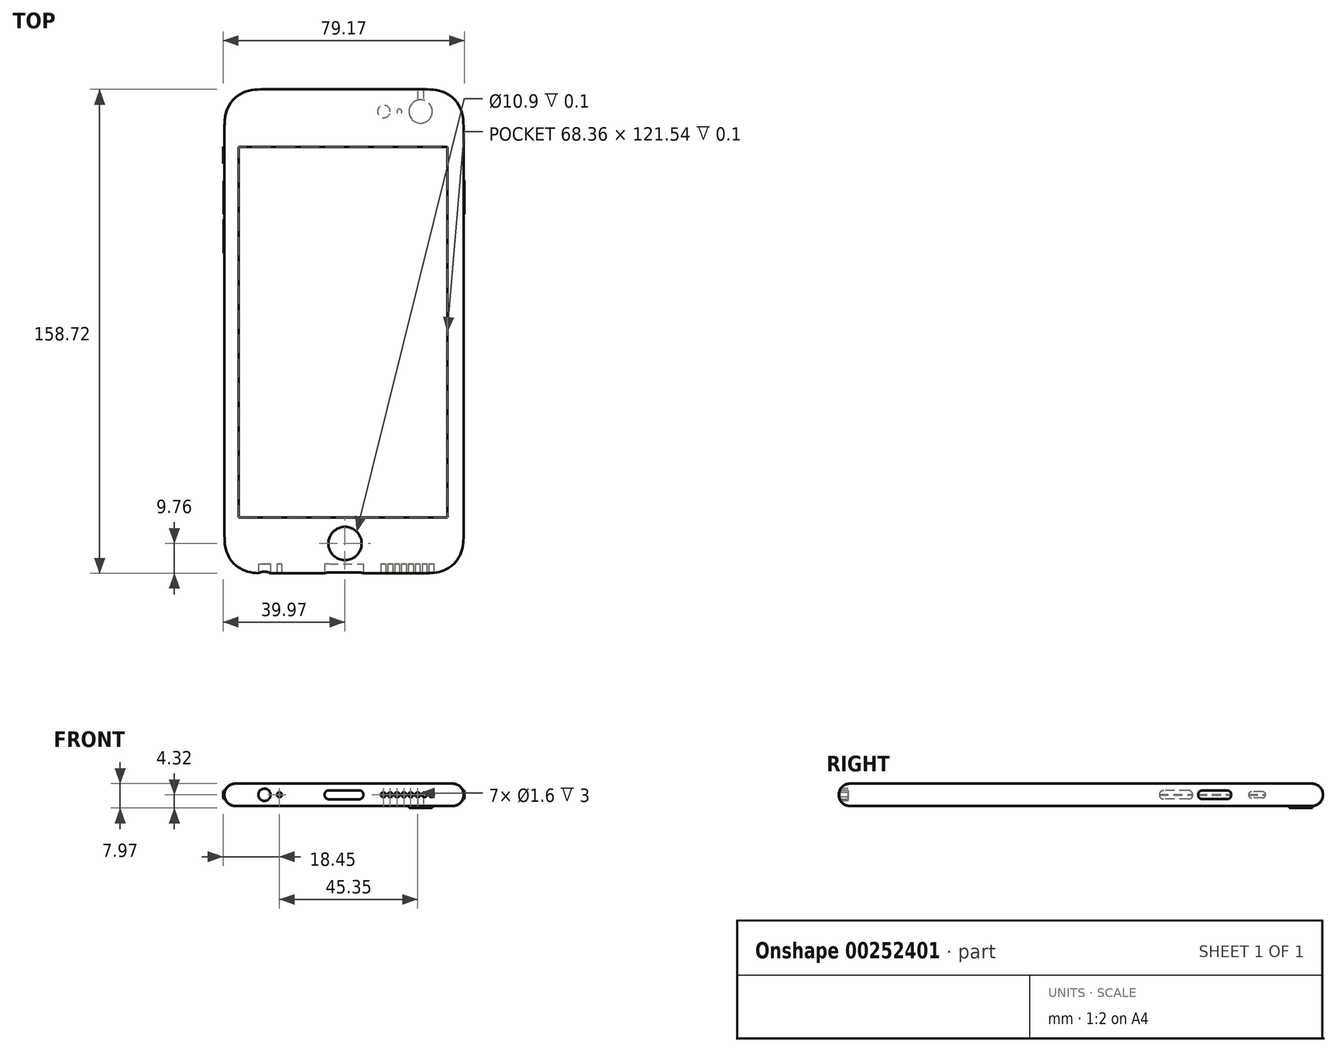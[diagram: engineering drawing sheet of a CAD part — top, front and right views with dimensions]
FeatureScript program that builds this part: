
annotation { "Feature Type Name" : "Feature", "Feature Type Description" : "" }
export const myFeature = defineFeature(function(context is Context, id is Id, definition is map)
    precondition{}
    {
        {
            var Q0;
            Q0=qCreatedBy(makeId("Top.planeOp"),FACE);
            var sketch = newSketch(context, id + "F0", { "sketchPlane" : qUnion([Q0])});
            skLineSegment(sketch, "E0.rect.bottom", {"start": v(25.09, -79.36) * mm, "end": v(-25.09, -79.36) * mm});
            skLineSegment(sketch, "E0.rect.top", {"start": v(25.09, 79.36) * mm, "end": v(-25.09, 79.36) * mm});
            skLineSegment(sketch, "E0.rect.left", {"start": v(39.22, -65.23) * mm, "end": v(39.22, 65.23) * mm});
            skLineSegment(sketch, "E0.rect.right", {"start": v(-39.22, -65.23) * mm, "end": v(-39.22, 65.23) * mm});
            skPoint(sketch, "E0.rect.middle", {"position": v(0, 0) * mm});
            skCircle(sketch, "E1", {"center": v(25.12, 72.09) * mm, "radius": 3.83 * mm});
            skCircle(sketch, "E2", {"center": v(18.16, 72.09) * mm, "radius": 0.8 * mm});
            skCircle(sketch, "E3", {"center": v(13.06, 72.09) * mm, "radius": 2.06 * mm});
            skLineSegment(sketch, "E4", {"start": v(-39.22, 72.1) * mm, "end": v(39.22, 72.1) * mm, "construction": true});
            skPoint(sketch, "E5.visualSharp", {"position": v(-39.22, 79.36) * mm});
            skFitSpline(sketch, "E6", {"points": [v(-25.09, 79.36) * mm, v(-29.02, 79.25) * mm, v(-32.83, 78.38) * mm, v(-36.09, 76.23) * mm, v(-38.24, 72.97) * mm, v(-39.1, 69.16) * mm, v(-39.22, 65.23) * mm], "startDerivative": vector(-8.98, 0) * mm, "endDerivative": vector(0, -8.98) * mm});
            skLineSegment(sketch, "E7", {"start": v(-25.09, 79.36) * mm, "end": v(-39.22, 79.36) * mm, "construction": true});
            skLineSegment(sketch, "E8", {"start": v(-39.22, 79.36) * mm, "end": v(-39.22, 65.23) * mm, "construction": true});
            skLineSegment(sketch, "E9", {"start": v(0, 79.36) * mm, "end": v(0, -79.36) * mm, "construction": true});
            skLineSegment(sketch, "E10", {"start": v(-39.22, 0) * mm, "end": v(39.22, 0) * mm, "construction": true});
            skFitSpline(sketch, "E11.MirrorCS", {"points": [v(25.09, 79.36) * mm, v(29.02, 79.25) * mm, v(32.83, 78.38) * mm, v(36.09, 76.23) * mm, v(38.24, 72.97) * mm, v(39.1, 69.16) * mm, v(39.22, 65.23) * mm], "startDerivative": vector(8.98, 0) * mm, "endDerivative": vector(0, -8.98) * mm});
            skFitSpline(sketch, "E12.MirrorCS", {"points": [v(-25.09, -79.36) * mm, v(-29.02, -79.25) * mm, v(-32.83, -78.38) * mm, v(-36.09, -76.23) * mm, v(-38.24, -72.97) * mm, v(-39.1, -69.16) * mm, v(-39.22, -65.23) * mm], "startDerivative": vector(-8.98, 0) * mm, "endDerivative": vector(0, 8.98) * mm});
            skFitSpline(sketch, "E13.MirrorCS", {"points": [v(25.09, -79.36) * mm, v(29.02, -79.25) * mm, v(32.83, -78.38) * mm, v(36.09, -76.23) * mm, v(38.24, -72.97) * mm, v(39.1, -69.16) * mm, v(39.22, -65.23) * mm], "startDerivative": vector(8.98, 0) * mm, "endDerivative": vector(0, 8.98) * mm});
            skCircle(sketch, "E14", {"center": v(0, 37.36) * mm, "radius": 11 * mm, "construction": true});
            skSolve(sketch);
        }
        {
            var Q0;
            Q0=makeQuery(id+"F0.imprint","IMPRINT",FACE,{"disambiguationData":[TD([[makeQuery(id+"F0.imprint","IMPRINT",EDGE,{"derivedFrom":sQuery(id+"F0.wireOp",EDGE,"E0.rect.bottom")}),-1.0]])]});
            var Q1;
            Q1=makeQuery(id+"F0.imprint","IMPRINT",FACE,{"disambiguationData":[TD([[makeQuery(id+"F0.imprint","IMPRINT",EDGE,{"derivedFrom":sQuery(id+"F0.wireOp",EDGE,"E1")}),1.0]])]});
            var Q2;
            Q2=makeQuery(id+"F0.imprint","IMPRINT",FACE,{"disambiguationData":[TD([[makeQuery(id+"F0.imprint","IMPRINT",EDGE,{"derivedFrom":sQuery(id+"F0.wireOp",EDGE,"E2")}),1.0]])]});
            var Q3;
            Q3=makeQuery(id+"F0.imprint","IMPRINT",FACE,{"disambiguationData":[TD([[makeQuery(id+"F0.imprint","IMPRINT",EDGE,{"derivedFrom":sQuery(id+"F0.wireOp",EDGE,"E3")}),1.0]])]});
            extrude(context, id + "F1", {"entities" : qUnion([Q0, Q1, Q2, Q3]), "depth" : 7.3 * mm});
        }
        {
            var Q0;
            Q0=makeQuery(id+"F0.imprint","IMPRINT",FACE,{"disambiguationData":[TD([[makeQuery(id+"F0.imprint","IMPRINT",EDGE,{"derivedFrom":sQuery(id+"F0.wireOp",EDGE,"E1")}),1.0]])]});
            extrude(context, id + "F2", {"entities" : qUnion([Q0]), "operationType" : NewBodyOperationType.ADD, "oppositeDirection" : true, "depth" : 0.67 * mm});
        }
        {
            var Q0;
            Q0=makeQuery(id+"F0.imprint","IMPRINT",FACE,{"disambiguationData":[TD([[makeQuery(id+"F0.imprint","IMPRINT",EDGE,{"derivedFrom":sQuery(id+"F0.wireOp",EDGE,"E3")}),1.0]])]});
            var Q1;
            Q1=makeQuery(id+"F0.imprint","IMPRINT",FACE,{"disambiguationData":[TD([[makeQuery(id+"F0.imprint","IMPRINT",EDGE,{"derivedFrom":sQuery(id+"F0.wireOp",EDGE,"E2")}),1.0]])]});
            extrude(context, id + "F3", {"entities" : qUnion([Q0, Q1]), "operationType" : NewBodyOperationType.REMOVE, "depth" : 0.1 * mm});
        }
        {
            var Q0;
            Q0=makeQuery(id+"F1.opExtrude","CAP_FACE",FACE,{"disambiguationData":[OSD([sQuery(id+"F0.wireOp",EDGE,"E0.rect.bottom"),sQuery(id+"F0.wireOp",EDGE,"E0.rect.top"),sQuery(id+"F0.wireOp",EDGE,"E0.rect.left"),sQuery(id+"F0.wireOp",EDGE,"E0.rect.right"),sQuery(id+"F0.wireOp",EDGE,"d7852d5b-fe0f-4a90-bdf2-04cff158e1f8.filletArc"),sQuery(id+"F0.wireOp",EDGE,"E5.filletArc"),sQuery(id+"F0.wireOp",EDGE,"7c06d2e9-cdf6-4879-9dee-aab3bc7c6033.filletArc"),sQuery(id+"F0.wireOp",EDGE,"93b3bdb9-dbb8-49f8-8f1e-002f612095da.filletArc")])],"isStart":false});
            var sketch = newSketch(context, id + "F4", { "sketchPlane" : qUnion([Q0])});
            skCircle(sketch, "E15", {"center": v(0.32, -69.6) * mm, "radius": 5.45 * mm});
            skLineSegment(sketch, "E16.bottom", {"start": v(-34.51, 60.44) * mm, "end": v(33.85, 60.44) * mm});
            skLineSegment(sketch, "E16.top", {"start": v(-34.5, -61.1) * mm, "end": v(33.85, -61.1) * mm});
            skLineSegment(sketch, "E16.left", {"start": v(-34.51, 60.44) * mm, "end": v(-34.5, -61.1) * mm});
            skLineSegment(sketch, "E16.right", {"start": v(33.85, 60.44) * mm, "end": v(33.85, -61.1) * mm});
            skSolve(sketch);
        }
        {
            var Q0;
            Q0=makeQuery(id+"F4.imprint","IMPRINT",FACE,{"disambiguationData":[TD([[makeQuery(id+"F4.imprint","IMPRINT",EDGE,{"derivedFrom":sQuery(id+"F4.wireOp",EDGE,"E15")}),1.0]])]});
            extrude(context, id + "F5", {"entities" : qUnion([Q0]), "operationType" : NewBodyOperationType.REMOVE, "oppositeDirection" : true, "depth" : 0.1 * mm});
        }
        {
            var Q0;
            Q0=makeQuery(id+"F4.imprint","IMPRINT",FACE,{"disambiguationData":[TD([[makeQuery(id+"F4.imprint","IMPRINT",EDGE,{"derivedFrom":sQuery(id+"F4.wireOp",EDGE,"E16.bottom")}),-1.0]])]});
            extrude(context, id + "F6", {"entities" : qUnion([Q0]), "operationType" : NewBodyOperationType.REMOVE, "oppositeDirection" : true, "depth" : 0.1 * mm});
        }
        {
            var Q0;
            Q0=makeQuery(id+"F1.opExtrude","SWEPT_FACE",FACE,{"disambiguationData":[OSD([sQuery(id+"F0.wireOp",EDGE,"E0.rect.bottom")])]});
            var sketch = newSketch(context, id + "F7", { "sketchPlane" : qUnion([Q0])});
            skLineSegment(sketch, "E17.0", {"start": v(25.09, 7.3) * mm, "end": v(-25.09, 7.3) * mm, "construction": true});
            skLineSegment(sketch, "E17.1", {"start": v(25.09, 0) * mm, "end": v(-25.09, 0) * mm, "construction": true});
            skLineSegment(sketch, "E17.2", {"start": v(39.22, 7.3) * mm, "end": v(39.22, 0) * mm, "construction": true});
            skLineSegment(sketch, "E17.3", {"start": v(-39.22, 7.3) * mm, "end": v(-39.22, 0) * mm, "construction": true});
            skFitSpline(sketch, "E17.4", {"points": [v(-24.74, 7.3) * mm, v(-29.45, 7.3) * mm, v(-34.16, 7.3) * mm, v(-38.87, 7.3) * mm], "construction": true});
            skFitSpline(sketch, "E17.5", {"points": [v(-24.74, 0) * mm, v(-29.45, 0) * mm, v(-34.16, 0) * mm, v(-38.87, 0) * mm], "construction": true});
            skFitSpline(sketch, "E17.6", {"points": [v(24.74, 0) * mm, v(29.45, 0) * mm, v(34.16, 0) * mm, v(38.87, 0) * mm], "construction": true});
            skFitSpline(sketch, "E17.7", {"points": [v(24.74, 7.3) * mm, v(29.45, 7.3) * mm, v(34.16, 7.3) * mm, v(38.87, 7.3) * mm], "construction": true});
            skLineSegment(sketch, "E18", {"start": v(0, 7.3) * mm, "end": v(0, 0) * mm, "construction": true});
            skLineSegment(sketch, "E19", {"start": v(-39.22, 3.65) * mm, "end": v(-6.4, 3.65) * mm, "construction": true});
            skLineSegment(sketch, "E20", {"start": v(-4.92, 5.12) * mm, "end": v(4.92, 5.12) * mm});
            skLineSegment(sketch, "E21", {"start": v(-4.92, 2.17) * mm, "end": v(4.92, 2.17) * mm});
            skLineSegment(sketch, "E22", {"start": v(-6.4, 3.65) * mm, "end": v(39.22, 3.65) * mm, "construction": true});
            skArc(sketch, "E23", {"start": v(-4.92, 5.13) * mm, "mid": v(-6.4, 3.65) * mm, "end": v(-4.92, 2.17) * mm});
            skArc(sketch, "E24", {"start": v(-4.92, 2.17) * mm, "mid": v(-3.44, 3.65) * mm, "end": v(-4.92, 5.13) * mm, "construction": true});
            skArc(sketch, "E25", {"start": v(4.92, 5.13) * mm, "mid": v(5.96, 4.7) * mm, "end": v(6.4, 3.65) * mm});
            skArc(sketch, "E26", {"start": v(4.92, 2.17) * mm, "mid": v(3.44, 3.65) * mm, "end": v(4.92, 5.13) * mm, "construction": true});
            skArc(sketch, "E27", {"start": v(6.4, 3.65) * mm, "mid": v(5.96, 2.6) * mm, "end": v(4.92, 2.17) * mm});
            skCircle(sketch, "E28", {"center": v(-26.09, 3.65) * mm, "radius": 2 * mm});
            skCircle(sketch, "E29", {"center": v(-21.2, 3.65) * mm, "radius": 0.8 * mm});
            skCircle(sketch, "E30", {"center": v(12.9, 3.65) * mm, "radius": 0.8 * mm});
            skCircle(sketch, "E31.1.0.0", {"center": v(15.15, 3.65) * mm, "radius": 0.8 * mm});
            skCircle(sketch, "E31.2.0.0", {"center": v(17.4, 3.65) * mm, "radius": 0.8 * mm});
            skCircle(sketch, "E31.3.0.0", {"center": v(19.65, 3.65) * mm, "radius": 0.8 * mm});
            skCircle(sketch, "E31.4.0.0", {"center": v(21.9, 3.65) * mm, "radius": 0.8 * mm});
            skCircle(sketch, "E31.5.0.0", {"center": v(24.15, 3.65) * mm, "radius": 0.8 * mm});
            skCircle(sketch, "E31.6.0.0", {"center": v(26.4, 3.65) * mm, "radius": 0.8 * mm});
            skCircle(sketch, "E31.7.0.0", {"center": v(28.65, 3.65) * mm, "radius": 0.8 * mm});
            skLineSegment(sketch, "E31.direction1", {"start": v(12.9, 3.65) * mm, "end": v(15.15, 3.65) * mm, "construction": true});
            skPoint(sketch, "E32", {"position": v(12.1, 3.65) * mm});
            skPoint(sketch, "E33", {"position": v(29.45, 3.65) * mm});
            skLineSegment(sketch, "E34.0", {"start": v(-25.09, 7.3) * mm, "end": v(-25.09, 0) * mm, "construction": true});
            skLineSegment(sketch, "E34.1", {"start": v(25.09, 7.3) * mm, "end": v(25.09, 0) * mm, "construction": true});
            skSolve(sketch);
        }
        {
            var Q0;
            Q0=makeQuery(id+"F1.opExtrude","SWEPT_FACE",FACE,{"disambiguationData":[OSD([sQuery(id+"F0.wireOp",EDGE,"E0.rect.left")])]});
            var sketch = newSketch(context, id + "F8", { "sketchPlane" : qUnion([Q0])});
            skLineSegment(sketch, "E35", {"start": v(-65.23, 2.25) * mm, "end": v(65.23, 2.25) * mm, "construction": true});
            skLineSegment(sketch, "E36", {"start": v(8.97, 4.69) * mm, "end": v(22.34, 4.7) * mm});
            skLineSegment(sketch, "E37", {"start": v(8.97, 2.25) * mm, "end": v(22.34, 2.25) * mm});
            skPoint(sketch, "E38", {"position": v(7.75, 3.47) * mm});
            skPoint(sketch, "E39", {"position": v(23.56, 3.47) * mm});
            skLineSegment(sketch, "E40", {"start": v(39.81, 2.25) * mm, "end": v(47.95, 2.25) * mm});
            skLineSegment(sketch, "E41", {"start": v(39.81, 5.05) * mm, "end": v(39.81, 5.05) * mm});
            skLineSegment(sketch, "E42", {"start": v(39.81, 3.65) * mm, "end": v(47.95, 3.65) * mm, "construction": true});
            skLineSegment(sketch, "E43", {"start": v(39.81, 5.05) * mm, "end": v(47.95, 5.05) * mm});
            skArc(sketch, "E44", {"start": v(47.95, 5.05) * mm, "mid": v(46.55, 3.65) * mm, "end": v(47.95, 2.25) * mm, "construction": true});
            skArc(sketch, "E45", {"start": v(47.95, 2.25) * mm, "mid": v(49.35, 3.65) * mm, "end": v(47.95, 5.05) * mm});
            skArc(sketch, "E46", {"start": v(39.81, 2.25) * mm, "mid": v(41.21, 3.65) * mm, "end": v(39.81, 5.05) * mm, "construction": true});
            skArc(sketch, "E47", {"start": v(39.81, 5.05) * mm, "mid": v(38.41, 3.65) * mm, "end": v(39.81, 2.25) * mm});
            skPoint(sketch, "E48", {"position": v(43.88, 3.65) * mm});
            skPoint(sketch, "E49", {"position": v(38.4, 3.65) * mm});
            skArc(sketch, "E50", {"start": v(8.97, 4.7) * mm, "mid": v(7.75, 3.47) * mm, "end": v(8.97, 2.25) * mm});
            skArc(sketch, "E51", {"start": v(8.97, 2.25) * mm, "mid": v(10.2, 3.47) * mm, "end": v(8.97, 4.7) * mm, "construction": true});
            skArc(sketch, "E52", {"start": v(22.34, 4.7) * mm, "mid": v(21.12, 3.47) * mm, "end": v(22.34, 2.25) * mm, "construction": true});
            skArc(sketch, "E53", {"start": v(22.34, 2.25) * mm, "mid": v(23.56, 3.47) * mm, "end": v(22.34, 4.7) * mm});
            skSolve(sketch);
        }
        {
            var Q0;
            Q0=makeQuery(id+"F1.opExtrude","SWEPT_FACE",FACE,{"disambiguationData":[OSD([sQuery(id+"F0.wireOp",EDGE,"E0.rect.right")])]});
            var sketch = newSketch(context, id + "F9", { "sketchPlane" : qUnion([Q0])});
            skLineSegment(sketch, "E54", {"start": v(-65.23, 3.63) * mm, "end": v(65.23, 3.63) * mm, "construction": true});
            skLineSegment(sketch, "E55", {"start": v(-60.58, 3.65) * mm, "end": v(-54.97, 3.65) * mm, "construction": true});
            skLineSegment(sketch, "E56", {"start": v(-59.6, 2.66) * mm, "end": v(-55.95, 2.66) * mm});
            skLineSegment(sketch, "E57", {"start": v(-59.6, 4.63) * mm, "end": v(-55.95, 4.63) * mm});
            skArc(sketch, "E58", {"start": v(-59.6, 2.66) * mm, "mid": v(-58.61, 3.64) * mm, "end": v(-59.6, 4.63) * mm, "construction": true});
            skArc(sketch, "E59", {"start": v(-59.6, 4.63) * mm, "mid": v(-60.58, 3.64) * mm, "end": v(-59.6, 2.66) * mm});
            skArc(sketch, "E60", {"start": v(-55.95, 2.66) * mm, "mid": v(-54.97, 3.65) * mm, "end": v(-55.95, 4.63) * mm});
            skArc(sketch, "E61", {"start": v(-55.95, 4.63) * mm, "mid": v(-56.94, 3.65) * mm, "end": v(-55.95, 2.66) * mm, "construction": true});
            skPoint(sketch, "E62.first.point", {"position": v(-49.28, 3.63) * mm});
            skPoint(sketch, "E62.second.point", {"position": v(-47.88, 2.23) * mm});
            skPoint(sketch, "E62.third.point", {"position": v(-47.88, 5.03) * mm});
            skPoint(sketch, "E63.first.point", {"position": v(-41.14, 3.63) * mm});
            skPoint(sketch, "E63.second.point", {"position": v(-39.74, 2.23) * mm});
            skPoint(sketch, "E63.third.point", {"position": v(-39.74, 5.03) * mm});
            skLineSegment(sketch, "E64", {"start": v(-47.88, 2.23) * mm, "end": v(-39.74, 2.23) * mm});
            skLineSegment(sketch, "E65", {"start": v(-47.88, 5.03) * mm, "end": v(-39.74, 5.03) * mm});
            skArc(sketch, "E66", {"start": v(-47.88, 5.03) * mm, "mid": v(-49.28, 3.63) * mm, "end": v(-47.88, 2.23) * mm});
            skArc(sketch, "E67", {"start": v(-47.88, 2.23) * mm, "mid": v(-46.48, 3.63) * mm, "end": v(-47.88, 5.03) * mm, "construction": true});
            skArc(sketch, "E68", {"start": v(-39.74, 2.23) * mm, "mid": v(-38.34, 3.63) * mm, "end": v(-39.74, 5.03) * mm});
            skArc(sketch, "E69", {"start": v(-39.74, 5.03) * mm, "mid": v(-41.14, 3.63) * mm, "end": v(-39.74, 2.23) * mm, "construction": true});
            skLineSegment(sketch, "E70", {"start": v(-47.88, 3.63) * mm, "end": v(-39.74, 3.63) * mm, "construction": true});
            skPoint(sketch, "E71", {"position": v(-43.81, 3.63) * mm});
            skLineSegment(sketch, "E72", {"start": v(-35.27, 2.23) * mm, "end": v(-27.13, 2.23) * mm});
            skLineSegment(sketch, "E73", {"start": v(-35.27, 5.03) * mm, "end": v(-27.13, 5.03) * mm});
            skPoint(sketch, "E74.third.point", {"position": v(-36.67, 3.63) * mm});
            skPoint(sketch, "E75.third.point", {"position": v(-25.73, 3.63) * mm});
            skLineSegment(sketch, "E76", {"start": v(-27.13, 3.63) * mm, "end": v(-35.27, 3.63) * mm, "construction": true});
            skPoint(sketch, "E77", {"position": v(-31.2, 3.63) * mm});
            skArc(sketch, "E78", {"start": v(-35.27, 2.23) * mm, "mid": v(-33.87, 3.63) * mm, "end": v(-35.27, 5.03) * mm, "construction": true});
            skArc(sketch, "E79", {"start": v(-35.27, 5.03) * mm, "mid": v(-36.67, 3.63) * mm, "end": v(-35.27, 2.23) * mm});
            skArc(sketch, "E80", {"start": v(-27.13, 5.03) * mm, "mid": v(-28.53, 3.63) * mm, "end": v(-27.13, 2.23) * mm, "construction": true});
            skArc(sketch, "E81", {"start": v(-27.13, 2.23) * mm, "mid": v(-25.73, 3.63) * mm, "end": v(-27.13, 5.03) * mm});
            skSolve(sketch);
        }
        {
            var Q0;
            Q0=makeQuery(id+"F1.opExtrude","CAP_EDGE",EDGE,{"disambiguationData":[OSD([sQuery(id+"F0.wireOp",EDGE,"E0.rect.top")])],"isStart":true});
            var Q1;
            Q1=makeQuery(id+"F1.opExtrude","CAP_EDGE",EDGE,{"disambiguationData":[OSD([sQuery(id+"F0.wireOp",EDGE,"E0.rect.top")])],"isStart":false});
            fillet(context, id + "F10", {"entities" : qUnion([Q0, Q1]), "radius" : (7.1 / 2) * mm, "tangentPropagation" : true, "allowEdgeOverflow" : false});
        }
        {
            var Q0;
            {var subQ0=makeQuery(id+"F1.opExtrude","SWEPT_EDGE",EDGE,{"disambiguationData":[OSD([sQuery(id+"F0.wireOp",EDGE,"E0.rect.bottom"),sQuery(id+"F0.wireOp",EDGE,"E12.MirrorCS")])]});var subQ1=sQuery(id+"F7.wireOp",EDGE,"E28");var subQ3=makeQuery(id+"F7.imprint","INTERSECT",VERTEX,{"disambiguationData":[OD(0.0)],"derivedFrom":[subQ0,subQ1]});Q0=makeQuery(id+"F7.imprint","IMPRINT",FACE,{"disambiguationData":[TD([[makeQuery(id+"F7.imprint","IMPRINT",EDGE,{"disambiguationData":[TD([[subQ3,-1.0]])],"derivedFrom":subQ1}),1.0]])]});}
            var Q1;
            Q1=makeQuery(id+"F7.imprint","IMPRINT",FACE,{"disambiguationData":[TD([[makeQuery(id+"F7.imprint","IMPRINT",EDGE,{"derivedFrom":sQuery(id+"F7.wireOp",EDGE,"E29")}),1.0]])]});
            var Q2;
            Q2=makeQuery(id+"F7.imprint","IMPRINT",FACE,{"disambiguationData":[TD([[makeQuery(id+"F7.imprint","IMPRINT",EDGE,{"derivedFrom":sQuery(id+"F7.wireOp",EDGE,"E20")}),-1.0]])]});
            var Q3;
            Q3=makeQuery(id+"F7.imprint","IMPRINT",FACE,{"disambiguationData":[TD([[makeQuery(id+"F7.imprint","IMPRINT",EDGE,{"derivedFrom":sQuery(id+"F7.wireOp",EDGE,"E30")}),1.0]])]});
            var Q4;
            Q4=makeQuery(id+"F7.imprint","IMPRINT",FACE,{"disambiguationData":[TD([[makeQuery(id+"F7.imprint","IMPRINT",EDGE,{"derivedFrom":sQuery(id+"F7.wireOp",EDGE,"E31.1.0.0")}),1.0]])]});
            var Q5;
            Q5=makeQuery(id+"F7.imprint","IMPRINT",FACE,{"disambiguationData":[TD([[makeQuery(id+"F7.imprint","IMPRINT",EDGE,{"derivedFrom":sQuery(id+"F7.wireOp",EDGE,"E31.2.0.0")}),1.0]])]});
            var Q6;
            Q6=makeQuery(id+"F7.imprint","IMPRINT",FACE,{"disambiguationData":[TD([[makeQuery(id+"F7.imprint","IMPRINT",EDGE,{"derivedFrom":sQuery(id+"F7.wireOp",EDGE,"E31.3.0.0")}),1.0]])]});
            var Q7;
            Q7=makeQuery(id+"F7.imprint","IMPRINT",FACE,{"disambiguationData":[TD([[makeQuery(id+"F7.imprint","IMPRINT",EDGE,{"derivedFrom":sQuery(id+"F7.wireOp",EDGE,"E31.4.0.0")}),1.0]])]});
            var Q8;
            Q8=makeQuery(id+"F7.imprint","IMPRINT",FACE,{"disambiguationData":[TD([[makeQuery(id+"F7.imprint","IMPRINT",EDGE,{"derivedFrom":sQuery(id+"F7.wireOp",EDGE,"E31.5.0.0")}),1.0]])]});
            var Q9;
            Q9=makeQuery(id+"F7.imprint","IMPRINT",FACE,{"disambiguationData":[TD([[makeQuery(id+"F7.imprint","IMPRINT",EDGE,{"derivedFrom":sQuery(id+"F7.wireOp",EDGE,"E31.6.0.0")}),1.0]])]});
            var Q10;
            Q10=makeQuery(id+"F7.imprint","IMPRINT",FACE,{"disambiguationData":[TD([[makeQuery(id+"F7.imprint","IMPRINT",EDGE,{"derivedFrom":sQuery(id+"F7.wireOp",EDGE,"E31.7.0.0")}),1.0]])]});
            var Q11;
            {var subQ0=makeQuery(id+"F1.opExtrude","SWEPT_EDGE",EDGE,{"disambiguationData":[OSD([sQuery(id+"F0.wireOp",EDGE,"E0.rect.bottom"),sQuery(id+"F0.wireOp",EDGE,"E12.MirrorCS")])]});var subQ1=sQuery(id+"F7.wireOp",EDGE,"E28");var subQ3=makeQuery(id+"F7.imprint","INTERSECT",VERTEX,{"disambiguationData":[OD(0.0)],"derivedFrom":[subQ0,subQ1]});Q11=makeQuery(id+"F7.imprint","IMPRINT",FACE,{"disambiguationData":[TD([[makeQuery(id+"F7.imprint","IMPRINT",EDGE,{"disambiguationData":[TD([[subQ3,1.0]])],"derivedFrom":subQ1}),1.0]])]});}
            extrude(context, id + "F11", {"entities" : qUnion([Q0, Q1, Q2, Q3, Q4, Q5, Q6, Q7, Q8, Q9, Q10, Q11]), "oppositeDirection" : true, "depth" : 3 * mm, "hasSecondDirection" : true, "secondDirectionOppositeDirection" : false, "secondDirectionDepth" : 1 * mm});
        }
        {
            var Q0;
            Q0=makeQuery(id+"F11.opExtrude","SWEPT_BODY",BODY,{"disambiguationData":[OSD([sQuery(id+"F7.wireOp",EDGE,"E28")])]});
            var Q1;
            Q1=makeQuery(id+"F11.opExtrude","SWEPT_BODY",BODY,{"disambiguationData":[OSD([sQuery(id+"F7.wireOp",EDGE,"E29")])]});
            var Q2;
            Q2=makeQuery(id+"F11.opExtrude","SWEPT_BODY",BODY,{"disambiguationData":[OSD([sQuery(id+"F7.wireOp",EDGE,"E30")])]});
            var Q3;
            Q3=makeQuery(id+"F11.opExtrude","SWEPT_BODY",BODY,{"disambiguationData":[OSD([sQuery(id+"F7.wireOp",EDGE,"E31.1.0.0")])]});
            var Q4;
            Q4=makeQuery(id+"F11.opExtrude","SWEPT_BODY",BODY,{"disambiguationData":[OSD([sQuery(id+"F7.wireOp",EDGE,"E31.2.0.0")])]});
            var Q5;
            Q5=makeQuery(id+"F11.opExtrude","SWEPT_BODY",BODY,{"disambiguationData":[OSD([sQuery(id+"F7.wireOp",EDGE,"E31.3.0.0")])]});
            var Q6;
            Q6=makeQuery(id+"F11.opExtrude","SWEPT_BODY",BODY,{"disambiguationData":[OSD([sQuery(id+"F7.wireOp",EDGE,"E31.4.0.0")])]});
            var Q7;
            Q7=makeQuery(id+"F11.opExtrude","SWEPT_BODY",BODY,{"disambiguationData":[OSD([sQuery(id+"F7.wireOp",EDGE,"E31.5.0.0")])]});
            var Q8;
            Q8=makeQuery(id+"F11.opExtrude","SWEPT_BODY",BODY,{"disambiguationData":[OSD([sQuery(id+"F7.wireOp",EDGE,"E31.6.0.0")])]});
            var Q9;
            Q9=makeQuery(id+"F11.opExtrude","SWEPT_BODY",BODY,{"disambiguationData":[OSD([sQuery(id+"F7.wireOp",EDGE,"E31.7.0.0")])]});
            var Q10;
            Q10=makeQuery(id+"F11.opExtrude","SWEPT_BODY",BODY,{"disambiguationData":[OSD([sQuery(id+"F7.wireOp",EDGE,"E20"),sQuery(id+"F7.wireOp",EDGE,"E21"),sQuery(id+"F7.wireOp",EDGE,"E23"),sQuery(id+"F7.wireOp",EDGE,"E25"),sQuery(id+"F7.wireOp",EDGE,"E27")])]});
            var Q11;
            Q11=makeQuery(id+"F1.opExtrude","SWEPT_BODY",BODY,{"disambiguationData":[OSD([sQuery(id+"F0.wireOp",EDGE,"E0.rect.bottom"),sQuery(id+"F0.wireOp",EDGE,"E0.rect.top"),sQuery(id+"F0.wireOp",EDGE,"E0.rect.left"),sQuery(id+"F0.wireOp",EDGE,"E0.rect.right"),sQuery(id+"F0.wireOp",EDGE,"E6"),sQuery(id+"F0.wireOp",EDGE,"E11.MirrorCS"),sQuery(id+"F0.wireOp",EDGE,"E12.MirrorCS"),sQuery(id+"F0.wireOp",EDGE,"E13.MirrorCS")])]});
            booleanBodies(context, id + "F12", {"operationType" : BooleanOperationType.SUBTRACTION, "tools" : qUnion([Q0, Q1, Q2, Q3, Q4, Q5, Q6, Q7, Q8, Q9, Q10]), "targets" : qUnion([Q11])});
        }
        {
            var Q0;
            Q0=makeQuery(id+"F8.imprint","IMPRINT",FACE,{"disambiguationData":[TD([[makeQuery(id+"F8.imprint","IMPRINT",EDGE,{"derivedFrom":sQuery(id+"F8.wireOp",EDGE,"E40")}),1.0]])]});
            extrude(context, id + "F13", {"entities" : qUnion([Q0]), "operationType" : NewBodyOperationType.ADD, "depth" : 0.3 * mm});
        }
        {
            var Q0;
            Q0=makeQuery(id+"F9.imprint","IMPRINT",FACE,{"disambiguationData":[TD([[makeQuery(id+"F9.imprint","IMPRINT",EDGE,{"derivedFrom":sQuery(id+"F9.wireOp",EDGE,"E72")}),1.0]])]});
            var Q1;
            Q1=makeQuery(id+"F9.imprint","IMPRINT",FACE,{"disambiguationData":[TD([[makeQuery(id+"F9.imprint","IMPRINT",EDGE,{"derivedFrom":sQuery(id+"F9.wireOp",EDGE,"E64")}),1.0]])]});
            extrude(context, id + "F14", {"entities" : qUnion([Q0, Q1]), "operationType" : NewBodyOperationType.ADD, "depth" : 0.3 * mm});
        }
        {
            var Q0;
            Q0=makeQuery(id+"F9.imprint","IMPRINT",FACE,{"disambiguationData":[TD([[makeQuery(id+"F9.imprint","IMPRINT",EDGE,{"derivedFrom":sQuery(id+"F9.wireOp",EDGE,"E56")}),1.0]])]});
            extrude(context, id + "F15", {"entities" : qUnion([Q0]), "operationType" : NewBodyOperationType.ADD, "depth" : 0.43 * mm});
        }
    });
